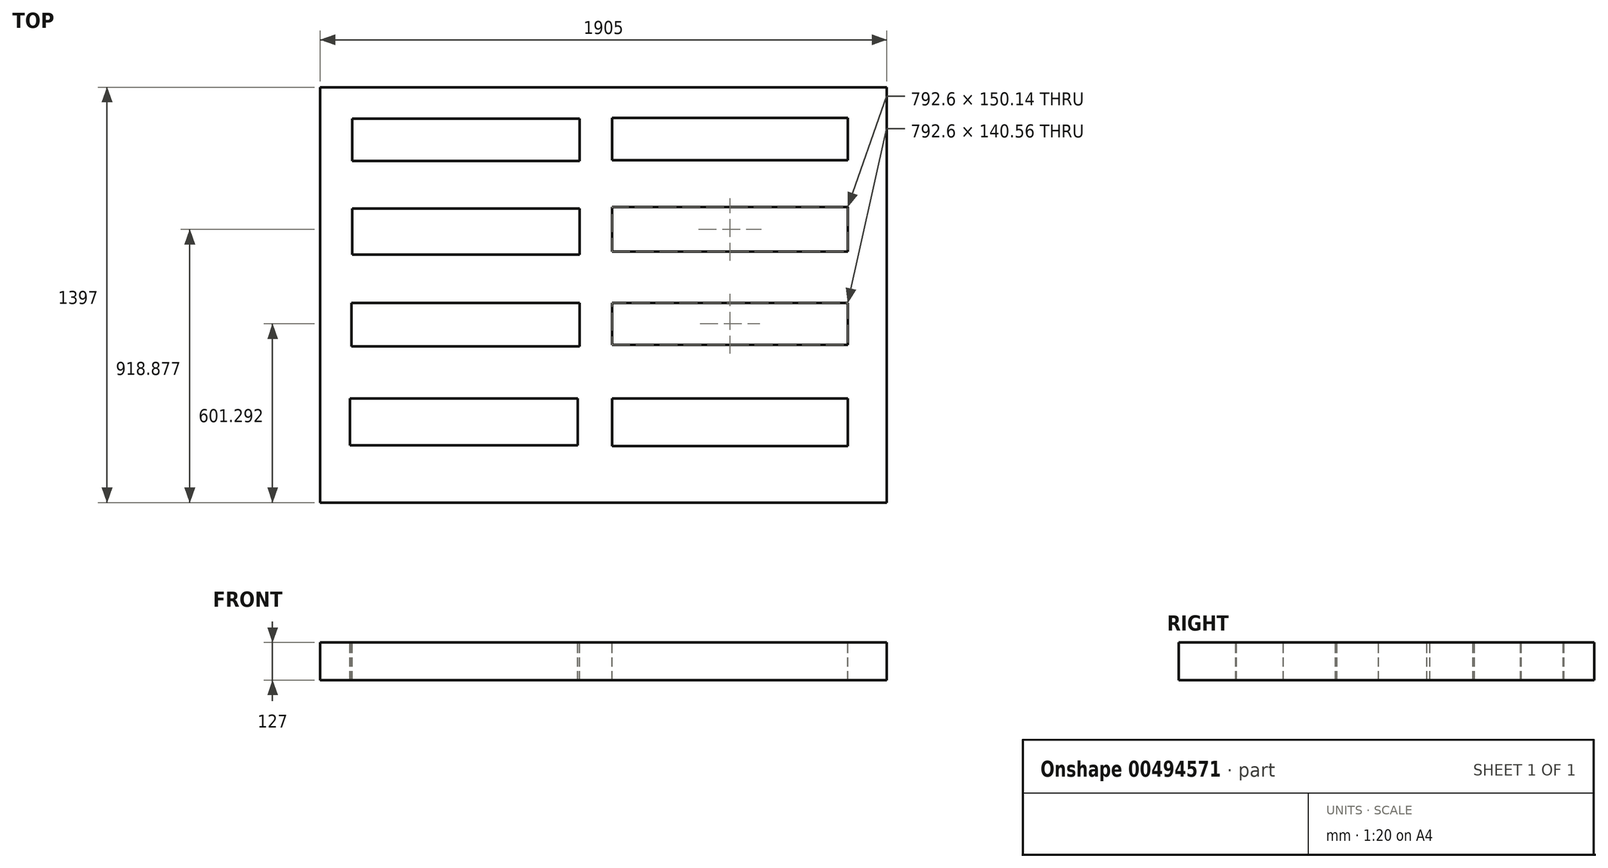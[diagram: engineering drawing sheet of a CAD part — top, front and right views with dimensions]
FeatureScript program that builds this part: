
annotation { "Feature Type Name" : "Feature", "Feature Type Description" : "" }
export const myFeature = defineFeature(function(context is Context, id is Id, definition is map)
    precondition{}
    {
        {
            var Q0;
            Q0=qCreatedBy(makeId("Top.planeOp"),FACE);
            var sketch = newSketch(context, id + "F0", { "sketchPlane" : qUnion([Q0])});
            skLineSegment(sketch, "E0.bottom", {"start": v(-981.03, 725.43) * mm, "end": v(923.97, 725.43) * mm});
            skLineSegment(sketch, "E0.top", {"start": v(-981.03, -671.57) * mm, "end": v(923.97, -671.57) * mm});
            skLineSegment(sketch, "E0.left", {"start": v(-981.03, 725.43) * mm, "end": v(-981.03, -671.57) * mm});
            skLineSegment(sketch, "E0.right", {"start": v(923.97, 725.43) * mm, "end": v(923.97, -671.57) * mm});
            skSolve(sketch);
        }
        {
            var Q0;
            Q0=makeQuery(id+"F0.imprint","IMPRINT",FACE,{"disambiguationData":[TD([[makeQuery(id+"F0.imprint","IMPRINT",EDGE,{"derivedFrom":sQuery(id+"F0.wireOp",EDGE,"E0.bottom")}),-1.0]])]});
            extrude(context, id + "F1", {"entities" : qUnion([Q0]), "depth" : 127 * mm});
        }
        {
            var Q0;
            Q0=makeQuery(id+"F1.opExtrude","CAP_FACE",FACE,{"disambiguationData":[OSD([sQuery(id+"F0.wireOp",EDGE,"E0.bottom"),sQuery(id+"F0.wireOp",EDGE,"E0.top"),sQuery(id+"F0.wireOp",EDGE,"E0.left"),sQuery(id+"F0.wireOp",EDGE,"E0.right")])],"isStart":false});
            var sketch = newSketch(context, id + "F2", { "sketchPlane" : qUnion([Q0])});
            skLineSegment(sketch, "E1.bottom", {"start": v(-873.96, 620.16) * mm, "end": v(-108.24, 620.16) * mm});
            skLineSegment(sketch, "E1.top", {"start": v(-873.96, 477.52) * mm, "end": v(-108.24, 477.52) * mm});
            skLineSegment(sketch, "E1.left", {"start": v(-873.96, 620.16) * mm, "end": v(-873.96, 477.52) * mm});
            skLineSegment(sketch, "E1.right", {"start": v(-108.24, 620.16) * mm, "end": v(-108.24, 477.52) * mm});
            skLineSegment(sketch, "E2.bottom", {"start": v(-873.96, 317.37) * mm, "end": v(-108.24, 317.37) * mm});
            skLineSegment(sketch, "E2.top", {"start": v(-873.96, 162.23) * mm, "end": v(-108.24, 162.23) * mm});
            skLineSegment(sketch, "E2.left", {"start": v(-873.96, 317.37) * mm, "end": v(-873.96, 162.23) * mm});
            skLineSegment(sketch, "E2.right", {"start": v(-108.24, 317.37) * mm, "end": v(-108.24, 162.23) * mm});
            skLineSegment(sketch, "E3.bottom", {"start": v(-876.46, 0) * mm, "end": v(-108.24, 0) * mm});
            skLineSegment(sketch, "E3.top", {"start": v(-876.46, -145.56) * mm, "end": v(-108.24, -145.56) * mm});
            skLineSegment(sketch, "E3.left", {"start": v(-876.46, 0) * mm, "end": v(-876.46, -145.56) * mm});
            skLineSegment(sketch, "E3.right", {"start": v(-108.24, 0) * mm, "end": v(-108.24, -145.56) * mm});
            skLineSegment(sketch, "E4.bottom", {"start": v(0, 622.66) * mm, "end": v(792.6, 622.66) * mm});
            skLineSegment(sketch, "E4.top", {"start": v(0, 480.02) * mm, "end": v(792.6, 480.02) * mm});
            skLineSegment(sketch, "E4.left", {"start": v(0, 622.66) * mm, "end": v(0, 480.02) * mm});
            skLineSegment(sketch, "E4.right", {"start": v(792.6, 622.66) * mm, "end": v(792.6, 480.02) * mm});
            skLineSegment(sketch, "E5.bottom", {"start": v(0, 322.38) * mm, "end": v(792.6, 322.38) * mm});
            skLineSegment(sketch, "E5.top", {"start": v(0, 172.24) * mm, "end": v(792.6, 172.24) * mm});
            skLineSegment(sketch, "E5.left", {"start": v(0, 322.38) * mm, "end": v(0, 172.24) * mm});
            skLineSegment(sketch, "E5.right", {"start": v(792.6, 322.38) * mm, "end": v(792.6, 172.24) * mm});
            skLineSegment(sketch, "E6.bottom", {"start": v(0, 0) * mm, "end": v(792.6, 0) * mm});
            skLineSegment(sketch, "E6.top", {"start": v(0, -140.56) * mm, "end": v(792.6, -140.56) * mm});
            skLineSegment(sketch, "E6.left", {"start": v(0, 0) * mm, "end": v(0, -140.56) * mm});
            skLineSegment(sketch, "E6.right", {"start": v(792.6, 0) * mm, "end": v(792.6, -140.56) * mm});
            skLineSegment(sketch, "E7.bottom", {"start": v(0, -320.72) * mm, "end": v(792.6, -320.72) * mm});
            skLineSegment(sketch, "E7.top", {"start": v(0, -480.87) * mm, "end": v(792.6, -480.87) * mm});
            skLineSegment(sketch, "E7.left", {"start": v(0, -320.72) * mm, "end": v(0, -480.87) * mm});
            skLineSegment(sketch, "E7.right", {"start": v(792.6, -320.72) * mm, "end": v(792.6, -480.87) * mm});
            skLineSegment(sketch, "E8.bottom", {"start": v(-115.76, -320.72) * mm, "end": v(-881.47, -320.72) * mm});
            skLineSegment(sketch, "E8.top", {"start": v(-115.76, -478.37) * mm, "end": v(-881.47, -478.37) * mm});
            skLineSegment(sketch, "E8.left", {"start": v(-115.76, -320.72) * mm, "end": v(-115.76, -478.37) * mm});
            skLineSegment(sketch, "E8.right", {"start": v(-881.47, -320.72) * mm, "end": v(-881.47, -478.37) * mm});
            skSolve(sketch);
        }
        {
            var Q0;
            Q0=makeQuery(id+"F2.imprint","IMPRINT",FACE,{"disambiguationData":[TD([[makeQuery(id+"F2.imprint","IMPRINT",EDGE,{"derivedFrom":sQuery(id+"F2.wireOp",EDGE,"E1.bottom")}),-1.0]])]});
            var Q1;
            Q1=makeQuery(id+"F2.imprint","IMPRINT",FACE,{"disambiguationData":[TD([[makeQuery(id+"F2.imprint","IMPRINT",EDGE,{"derivedFrom":sQuery(id+"F2.wireOp",EDGE,"E4.bottom")}),-1.0]])]});
            var Q2;
            Q2=makeQuery(id+"F2.imprint","IMPRINT",FACE,{"disambiguationData":[TD([[makeQuery(id+"F2.imprint","IMPRINT",EDGE,{"derivedFrom":sQuery(id+"F2.wireOp",EDGE,"E2.bottom")}),-1.0]])]});
            var Q3;
            Q3=makeQuery(id+"F2.imprint","IMPRINT",FACE,{"disambiguationData":[TD([[makeQuery(id+"F2.imprint","IMPRINT",EDGE,{"derivedFrom":sQuery(id+"F2.wireOp",EDGE,"E5.bottom")}),-1.0]])]});
            var Q4;
            Q4=makeQuery(id+"F2.imprint","IMPRINT",FACE,{"disambiguationData":[TD([[makeQuery(id+"F2.imprint","IMPRINT",EDGE,{"derivedFrom":sQuery(id+"F2.wireOp",EDGE,"E6.bottom")}),-1.0]])]});
            var Q5;
            Q5=makeQuery(id+"F2.imprint","IMPRINT",FACE,{"disambiguationData":[TD([[makeQuery(id+"F2.imprint","IMPRINT",EDGE,{"derivedFrom":sQuery(id+"F2.wireOp",EDGE,"E3.bottom")}),-1.0]])]});
            var Q6;
            Q6=makeQuery(id+"F2.imprint","IMPRINT",FACE,{"disambiguationData":[TD([[makeQuery(id+"F2.imprint","IMPRINT",EDGE,{"derivedFrom":sQuery(id+"F2.wireOp",EDGE,"E8.bottom")}),1.0]])]});
            var Q7;
            Q7=makeQuery(id+"F2.imprint","IMPRINT",FACE,{"disambiguationData":[TD([[makeQuery(id+"F2.imprint","IMPRINT",EDGE,{"derivedFrom":sQuery(id+"F2.wireOp",EDGE,"E7.bottom")}),-1.0]])]});
            extrude(context, id + "F3", {"entities" : qUnion([Q0, Q1, Q2, Q3, Q4, Q5, Q6, Q7]), "operationType" : NewBodyOperationType.REMOVE, "endBound" : BoundingType.THROUGH_ALL, "oppositeDirection" : true, "depth" : 25.4 * mm});
        }
    });
